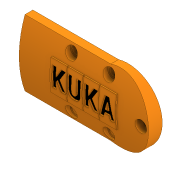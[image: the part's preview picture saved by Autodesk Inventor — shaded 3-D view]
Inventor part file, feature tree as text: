
AUTODESK INVENTOR PART (.ipt)
format: ipt  version: 2020 (Build 240168000, 168)  size: 511,488 bytes
history: native  units: in
note: dims shown in document units (in); Inventor stores cm internally (conversion verified against a paired STEP export)
features: sketch x11, extrude x10, plane x2, fillet x1, emboss x1, projected_geometry x1
ambient origin geometry x8: Origin, YZ Plane, XZ Plane, XY Plane, X Axis, Y Axis, Z Axis, Center Point
bodies: Solid1 (feature_tree)
feature tree (26):
  extrude  "Extrusion1"  Depth=0.1575in
  extrude  "Extrusion2"  Depth=0.2362in
  extrude  "Extrusion3"  Depth=0.2362in
  fillet  "Fillet1"  Radius=0.2264in
  plane  "Work Plane1"
  extrude  "Extrusion4"  Depth=0.1969in
  sketch  "Sketch5"  dims[d11=0.0in d12=0.0in d13=0.0787in]
  extrude  "Extrusion5"  Depth=0.0787in
  extrude  "Extrusion6"  Depth=0.5512in
  extrude  "Extrusion7"  Depth=0.9843in
  emboss  "Emboss1"
  plane  "Work Plane2"
  extrude  "Extrusion8"  Depth=0.0197in
  extrude  "Extrusion9"  Depth=0.0197in
  extrude  "Extrusion10"  Depth=0.0787in TaperAngle=0.0deg
  sketch  "Sketch1"  dims[d0=0.1575in d1=0.2362in]
  sketch  "Sketch2"  dims[d2=0.2362in d3=0.2362in]
  sketch  "Sketch3"  dims[d4=0.2362in d5=0.2362in d6=0.2264in d7=0.0in]
  sketch  "Sketch4"  dims[d8=0.1969in d9=0.0in d10=0.1969in]
  projected_geometry  "Projected Loop1"
  sketch  "Sketch6"  dims[d14=0.5512in d15=0.5512in]
  sketch  "Sketch7"  dims[d16=0.9843in d17=0.9843in]
  sketch  "Sketch8"  dims[d18=0.0787in d19=0.0in d20=0.0197in]
  sketch  "Sketch9"  dims[d21=0.0197in d22=0.0197in]
  sketch  "Sketch10"  dims[d23=0.0in d24=0.0in d25=0.0787in d26=0.0in]
  sketch  "Sketch11"  dims[d27=0.0in d28=0.0in d29=0.0394in d30=0.0in d31=0.3543in d32=0.3543in d33=0.3543in d34=0.3543in d35=0.3543in d36=0.4724in d37=0.0in d38=0.315in d39=0.5512in d40=0.0984in d41=0.0in d42=0.0984in d43=0.0in]
